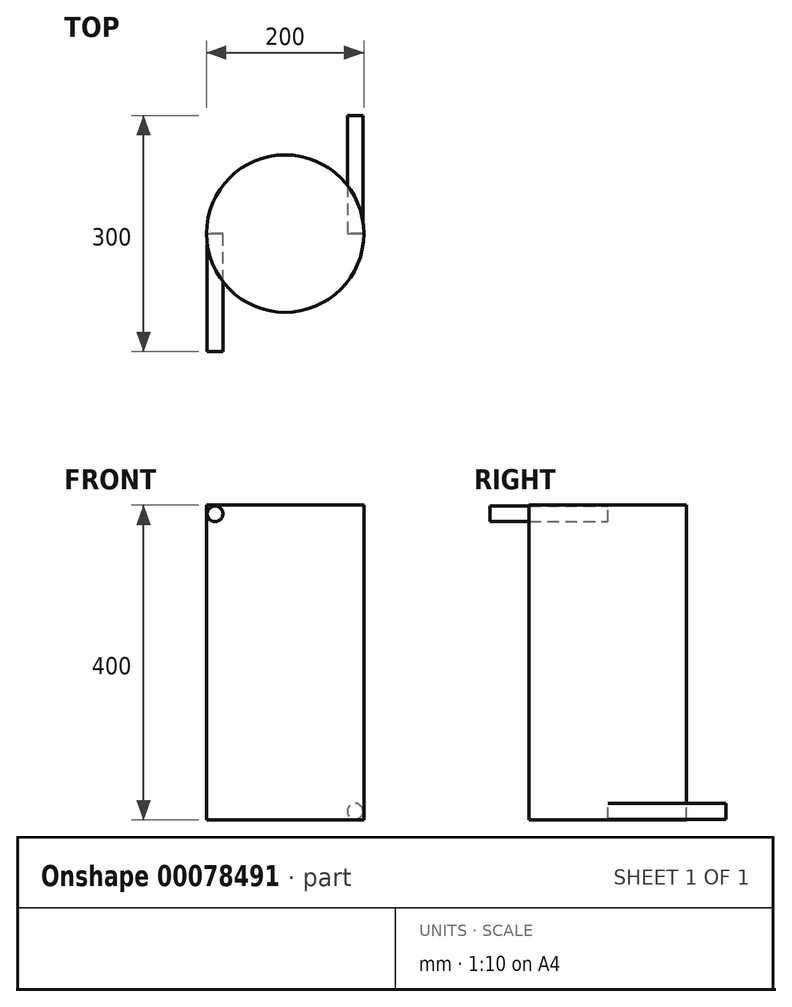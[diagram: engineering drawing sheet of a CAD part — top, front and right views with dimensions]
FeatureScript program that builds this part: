
annotation { "Feature Type Name" : "Feature", "Feature Type Description" : "" }
export const myFeature = defineFeature(function(context is Context, id is Id, definition is map)
    precondition{}
    {
        {
            var Q0;
            Q0=qCreatedBy(makeId("Top.planeOp"),FACE);
            cPlane(context, id + "F0", {"entities" : qUnion([Q0]), "cplaneType" : CPlaneType.OFFSET, "offset" : 200 * mm, "width" : 150 * mm, "height" : 150 * mm});
        }
        {
            var Q0;
            Q0=qCreatedBy(id+"F0.planeOp",FACE);
            var sketch = newSketch(context, id + "F1", { "sketchPlane" : qUnion([Q0])});
            skCircle(sketch, "E0", {"center": v(0, 0) * mm, "radius": 100 * mm});
            skSolve(sketch);
        }
        {
            var Q0;
            Q0=makeQuery(id+"F1.imprint","IMPRINT",FACE,{"disambiguationData":[TD([[makeQuery(id+"F1.imprint","IMPRINT",EDGE,{"derivedFrom":sQuery(id+"F1.wireOp",EDGE,"E0")}),1.0]])]});
            extrude(context, id + "F2", {"entities" : qUnion([Q0]), "oppositeDirection" : true, "depth" : 400 * mm});
        }
        {
            var Q0;
            Q0=qCreatedBy(makeId("Front.planeOp"),FACE);
            var sketch = newSketch(context, id + "F3", { "sketchPlane" : qUnion([Q0])});
            skCircle(sketch, "E1", {"center": v(-89, 189) * mm, "radius": 10 * mm});
            skSolve(sketch);
        }
        {
            var Q0;
            Q0=makeQuery(id+"F3.imprint","IMPRINT",FACE,{"disambiguationData":[TD([[makeQuery(id+"F3.imprint","IMPRINT",EDGE,{"derivedFrom":sQuery(id+"F3.wireOp",EDGE,"E1")}),1.0]])]});
            extrude(context, id + "F4", {"entities" : qUnion([Q0]), "depth" : 150 * mm});
        }
        {
            var Q0;
            Q0=qCreatedBy(makeId("Front.planeOp"),FACE);
            var sketch = newSketch(context, id + "F5", { "sketchPlane" : qUnion([Q0])});
            skCircle(sketch, "E2", {"center": v(89, -189) * mm, "radius": 10 * mm});
            skSolve(sketch);
        }
        {
            var Q0;
            Q0=makeQuery(id+"F5.imprint","IMPRINT",FACE,{"disambiguationData":[TD([[makeQuery(id+"F5.imprint","IMPRINT",EDGE,{"derivedFrom":sQuery(id+"F5.wireOp",EDGE,"E2")}),1.0]])]});
            extrude(context, id + "F6", {"entities" : qUnion([Q0]), "oppositeDirection" : true, "depth" : 150 * mm});
        }
    });
